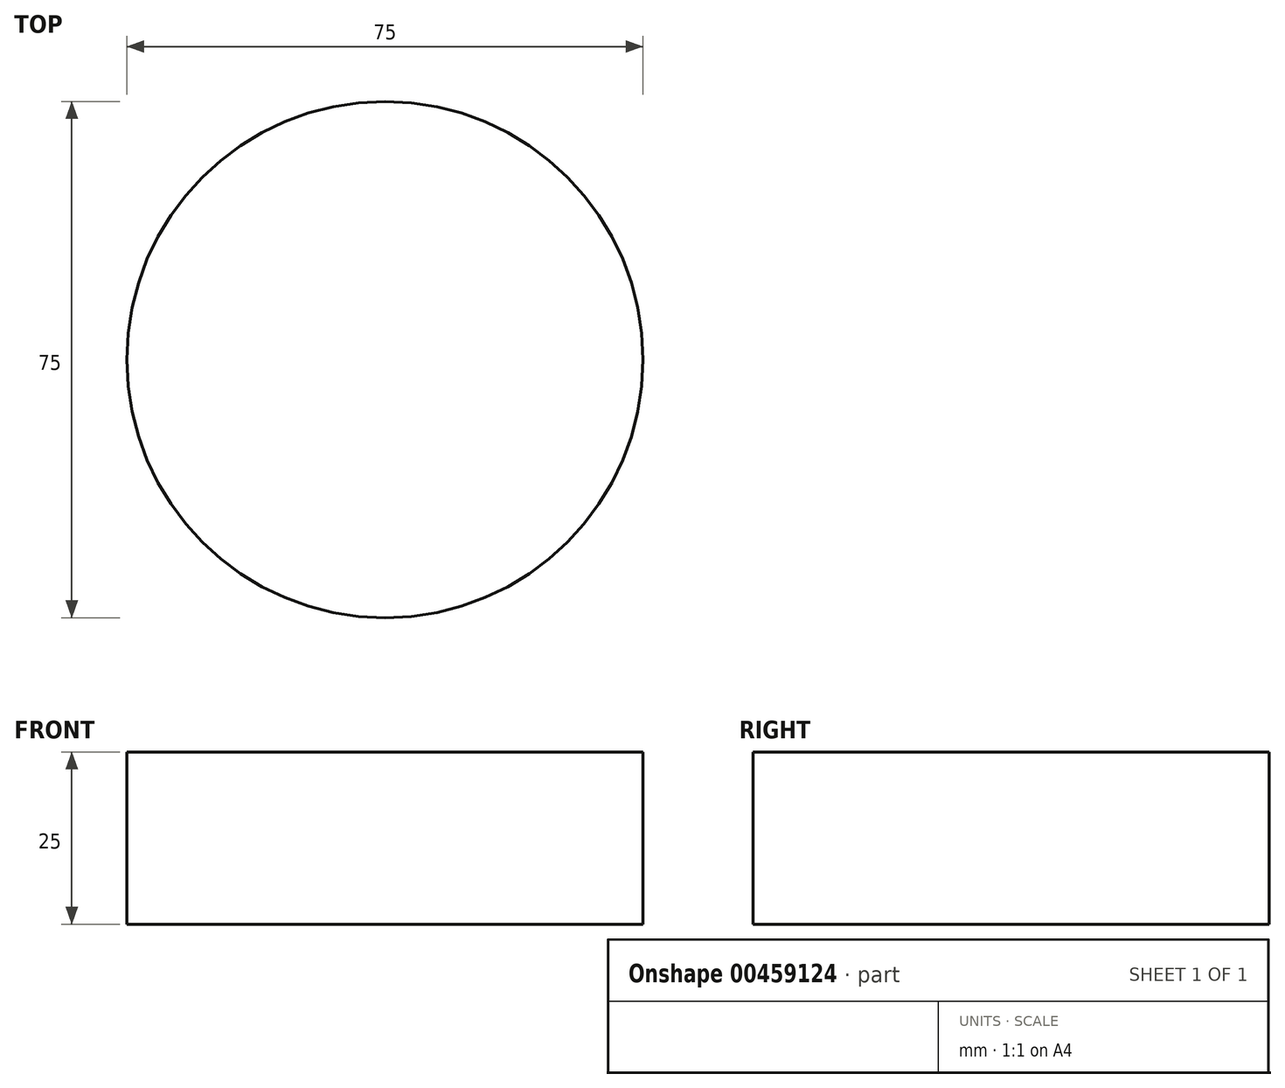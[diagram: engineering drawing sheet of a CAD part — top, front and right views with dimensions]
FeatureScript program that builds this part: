
annotation { "Feature Type Name" : "Feature", "Feature Type Description" : "" }
export const myFeature = defineFeature(function(context is Context, id is Id, definition is map)
    precondition{}
    {
        {
            var Q0;
            Q0=qCreatedBy(makeId("Top.planeOp"),FACE);
            var sketch = newSketch(context, id + "F0", { "sketchPlane" : qUnion([Q0])});
            skCircle(sketch, "E0", {"center": v(0, 0) * mm, "radius": 37.5 * mm});
            skSolve(sketch);
        }
        {
            var Q0;
            Q0=makeQuery(id+"F0.imprint","IMPRINT",FACE,{"disambiguationData":[TD([[makeQuery(id+"F0.imprint","IMPRINT",EDGE,{"derivedFrom":sQuery(id+"F0.wireOp",EDGE,"E0")}),1.0]])]});
            extrude(context, id + "F1", {"entities" : qUnion([Q0]), "depth" : 25 * mm});
        }
    });
